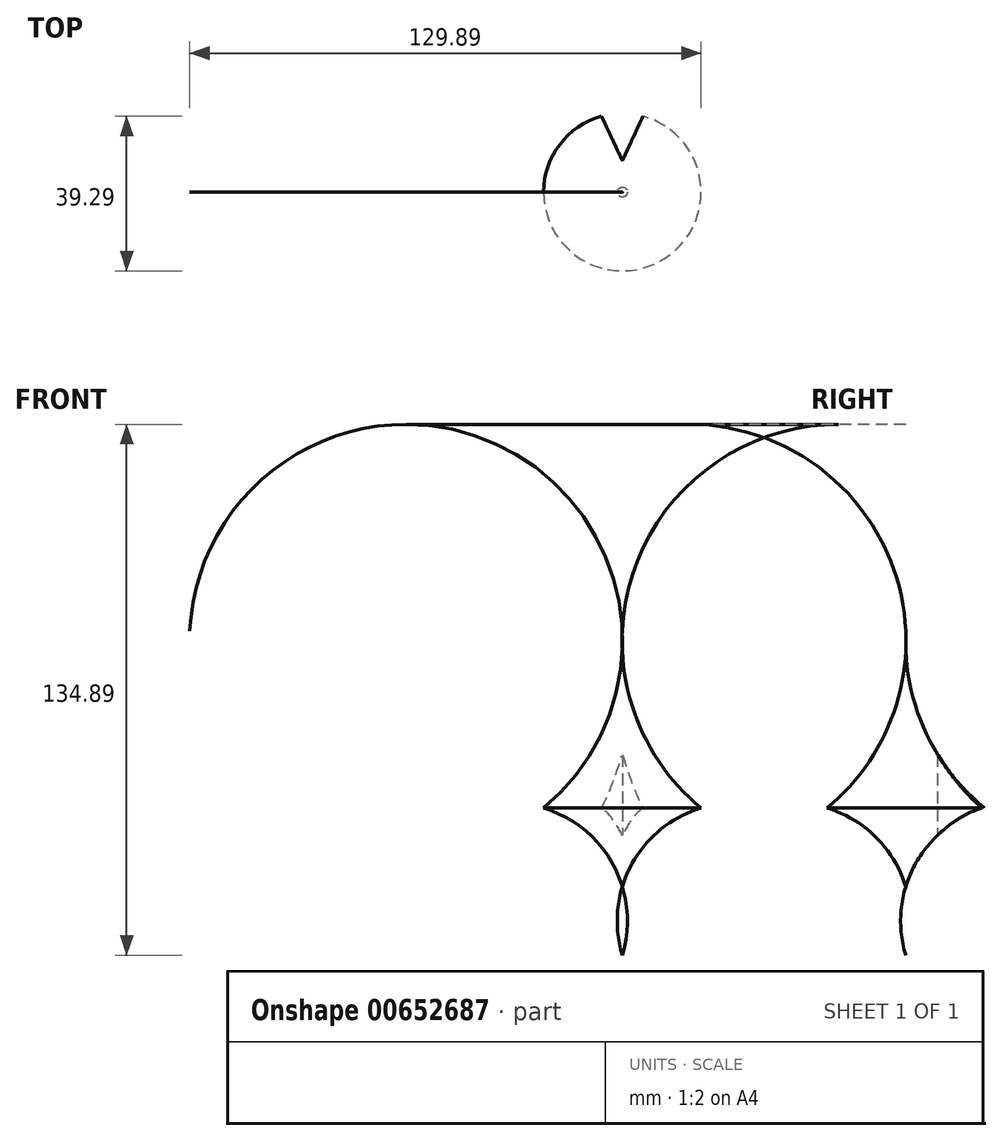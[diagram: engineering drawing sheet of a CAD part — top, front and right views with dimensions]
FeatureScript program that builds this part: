
annotation { "Feature Type Name" : "Feature", "Feature Type Description" : "" }
export const myFeature = defineFeature(function(context is Context, id is Id, definition is map)
    precondition{}
    {
        {
            var Q0;
            Q0=qCreatedBy(makeId("Front.planeOp"),FACE);
            var sketch = newSketch(context, id + "F0", { "sketchPlane" : qUnion([Q0])});
            skLineSegment(sketch, "E0", {"start": v(0, -37.37) * mm, "end": v(0, 68.05) * mm, "construction": true});
            skArc(sketch, "E1", {"start": v(20, 20) * mm, "mid": v(7.5, 12.5) * mm, "end": v(0, 0) * mm});
            skArc(sketch, "E2", {"start": v(0, 60) * mm, "mid": v(5.75, 37.88) * mm, "end": v(20, 20) * mm});
            skLineSegment(sketch, "E3", {"start": v(0, 60) * mm, "end": v(0, 0) * mm});
            skSolve(sketch);
        }
        {
            var Q0;
            Q0 = qSketchRegion(id + "F0", true);
            var Q1;
            Q1=sQuery(id+"F0.wireOp",EDGE,"E0");
            revolve(context, id + "F1", {"entities" : qUnion([Q0]), "axis" : qUnion([Q1]), "revolveType" : RevolveType.FULL});
        }
        {
            var Q0;
            Q0=qCreatedBy(makeId("Top.planeOp"),FACE);
            var sketch = newSketch(context, id + "F2", { "sketchPlane" : qUnion([Q0])});
            skCircle(sketch, "E4.0", {"center": v(0, 0) * mm, "radius": 20 * mm});
            skLineSegment(sketch, "E5", {"start": v(-5.27, 19.3) * mm, "end": v(0, 8) * mm});
            skLineSegment(sketch, "E6", {"start": v(0, 8) * mm, "end": v(5.27, 19.3) * mm});
            skLineSegment(sketch, "E7", {"start": v(0, 0) * mm, "end": v(0, 30.1) * mm, "construction": true});
            skSolve(sketch);
        }
        {
            var Q0;
            {var subQ0=sQuery(id+"F2.wireOp",EDGE,"E5");Q0=makeQuery(id+"F2.imprint","IMPRINT",FACE,{"disambiguationData":[TD([[makeQuery(id+"F2.imprint","IMPRINT",EDGE,{"derivedFrom":subQ0}),1.0]])]});}
            extrude(context, id + "F3", {"entities" : qUnion([Q0]), "operationType" : NewBodyOperationType.REMOVE, "depth" : 33.4 * mm, "offsetDistance" : 25 * mm});
        }
    });
